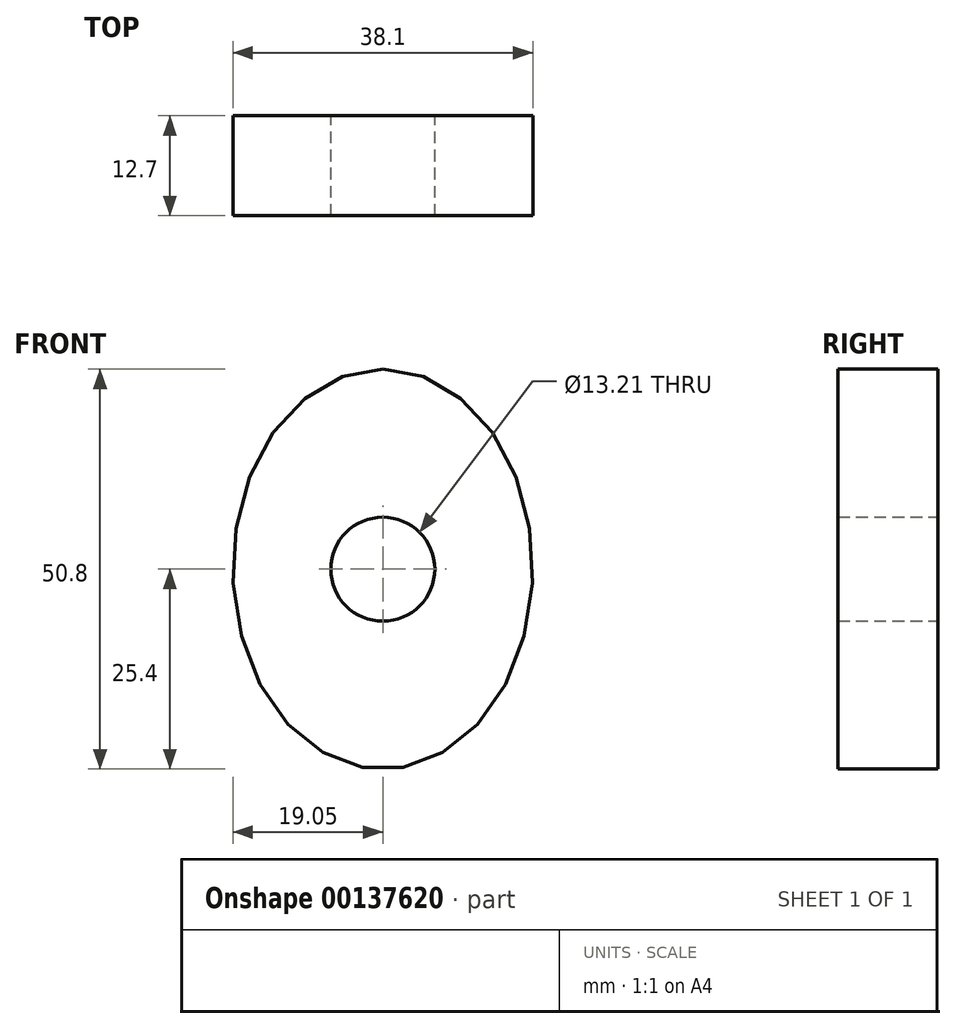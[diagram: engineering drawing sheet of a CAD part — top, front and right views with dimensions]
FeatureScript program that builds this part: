
annotation { "Feature Type Name" : "Feature", "Feature Type Description" : "" }
export const myFeature = defineFeature(function(context is Context, id is Id, definition is map)
    precondition{}
    {
        {
            var Q0;
            Q0=qCreatedBy(makeId("Front.planeOp"),FACE);
            var sketch = newSketch(context, id + "F0", { "sketchPlane" : qUnion([Q0])});
            skEllipse(sketch, "E0", {"center": v(0, 0) * mm, "majorRadius": 25.4 * mm, "minorRadius": 19.05 * mm, "majorAxis": v(0, 1)});
            skLineSegment(sketch, "E1", {"start": v(0, 25.4) * mm, "end": v(29.98, 25.4) * mm, "construction": true});
            skSolve(sketch);
        }
        {
            var Q0;
            Q0=makeQuery(id+"F0.imprint","IMPRINT",FACE,{"disambiguationData":[TD([[makeQuery(id+"F0.imprint","IMPRINT",EDGE,{"derivedFrom":sQuery(id+"F0.wireOp",EDGE,"E0")}),1.0]])]});
            extrude(context, id + "F1", {"entities" : qUnion([Q0]), "depth" : 12.7 * mm});
        }
        {
            var Q0;
            Q0=makeQuery(id+"F1.opExtrude","CAP_FACE",FACE,{"disambiguationData":[OSD([sQuery(id+"F0.wireOp",EDGE,"E0")])],"isStart":false});
            var sketch = newSketch(context, id + "F2", { "sketchPlane" : qUnion([Q0])});
            skCircle(sketch, "E2", {"center": v(0, 0) * mm, "radius": 6.6 * mm});
            skSolve(sketch);
        }
        {
            var Q0;
            Q0=makeQuery(id+"F2.imprint","IMPRINT",FACE,{"disambiguationData":[TD([[makeQuery(id+"F2.imprint","IMPRINT",EDGE,{"derivedFrom":sQuery(id+"F2.wireOp",EDGE,"E2")}),1.0]])]});
            var Q1;
            Q1=sQuery(id+"F2.wireOp",EDGE,"E2");
            extrude(context, id + "F3", {"entities" : qUnion([Q0]), "operationType" : NewBodyOperationType.REMOVE, "surfaceEntities" : qUnion([Q1]), "endBound" : BoundingType.SYMMETRIC, "depth" : 25.4 * mm});
        }
    });
